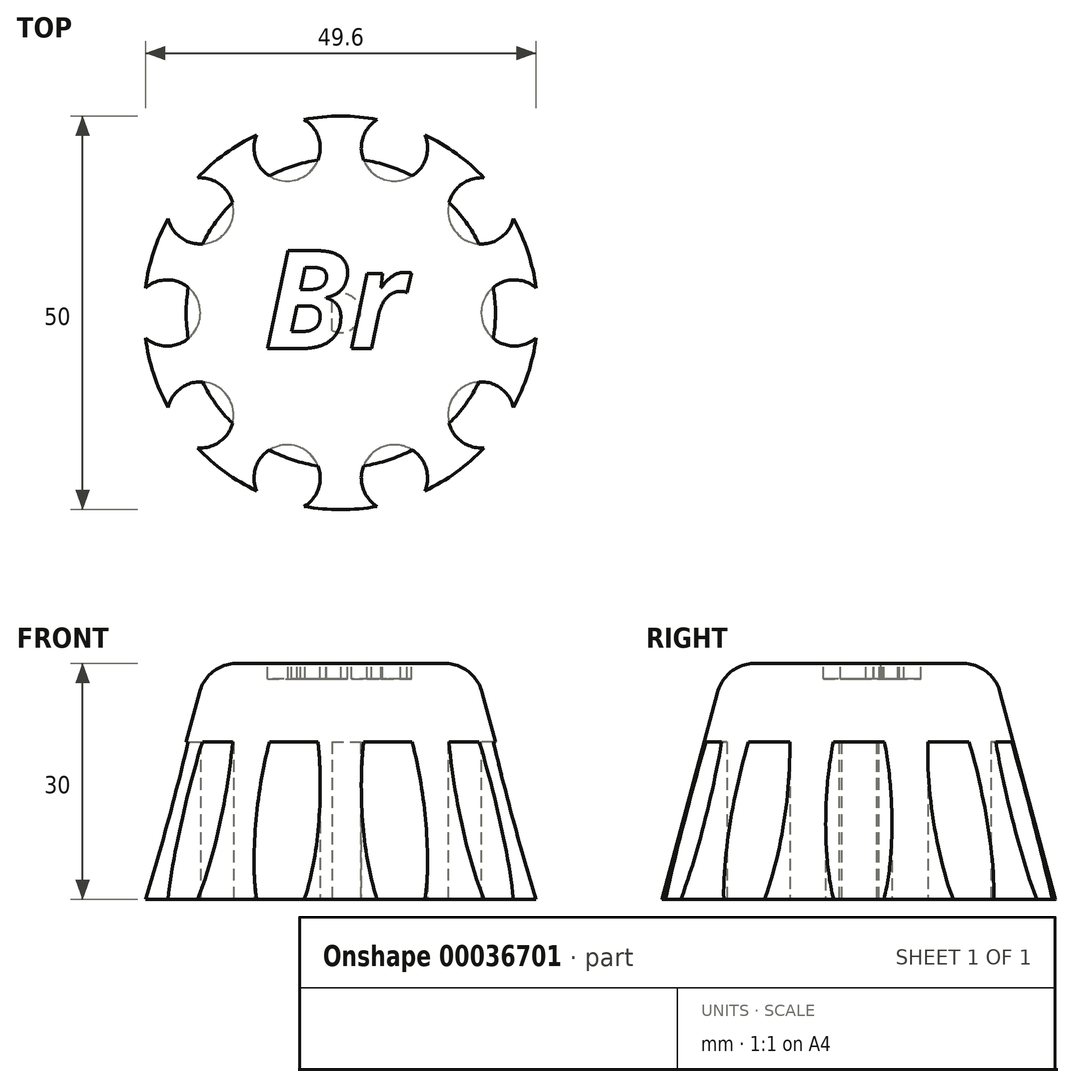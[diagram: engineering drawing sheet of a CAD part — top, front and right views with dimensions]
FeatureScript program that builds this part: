
annotation { "Feature Type Name" : "Feature", "Feature Type Description" : "" }
export const myFeature = defineFeature(function(context is Context, id is Id, definition is map)
    precondition{}
    {
        {
            var Q0;
            Q0=qCreatedBy(makeId("Top.planeOp"),FACE);
            var sketch = newSketch(context, id + "F0", { "sketchPlane" : qUnion([Q0])});
            skCircle(sketch, "E0", {"center": v(0, 0) * mm, "radius": 25 * mm});
            skSolve(sketch);
        }
        {
            var Q0;
            Q0=qSketchRegion(id+"F0",true);
            extrude(context, id + "F1", {"entities" : qUnion([Q0]), "depth" : 30 * mm, "hasDraft" : true, "draftAngle" : 15 * degree, "draftPullDirection" : true});
        }
        {
            var Q0;
            Q0=qCreatedBy(makeId("Top.planeOp"),FACE);
            var sketch = newSketch(context, id + "F2", { "sketchPlane" : qUnion([Q0])});
            skArc(sketch, "E1", {"start": v(-1.13, -2.23) * mm, "mid": v(2.5, 0) * mm, "end": v(-1.13, 2.23) * mm});
            skLineSegment(sketch, "E2", {"start": v(-1.13, -2.23) * mm, "end": v(-1.13, 2.23) * mm});
            skSolve(sketch);
        }
        {
            var Q0;
            Q0=qSketchRegion(id+"F2",true);
            extrude(context, id + "F3", {"entities" : qUnion([Q0]), "operationType" : NewBodyOperationType.REMOVE, "depth" : 20 * mm});
        }
        {
            var Q0;
            Q0=qCreatedBy(makeId("Top.planeOp"),FACE);
            var sketch = newSketch(context, id + "F4", { "sketchPlane" : qUnion([Q0])});
            skPoint(sketch, "E3.center", {"position": v(0, 0) * mm});
            skCircle(sketch, "E4", {"center": v(0, 0) * mm, "radius": 22.04 * mm, "construction": true});
            skCircle(sketch, "E5", {"center": v(22.04, 0) * mm, "radius": 4.2 * mm});
            skCircle(sketch, "E6.1.0", {"center": v(17.83, 12.96) * mm, "radius": 4.2 * mm});
            skCircle(sketch, "E6.2.0", {"center": v(6.81, 20.96) * mm, "radius": 4.2 * mm});
            skCircle(sketch, "E6.3.0", {"center": v(-6.81, 20.96) * mm, "radius": 4.2 * mm});
            skCircle(sketch, "E6.4.0", {"center": v(-17.83, 12.96) * mm, "radius": 4.2 * mm});
            skCircle(sketch, "E6.5.0", {"center": v(-22.04, 0) * mm, "radius": 4.2 * mm});
            skCircle(sketch, "E6.6.0", {"center": v(-17.83, -12.96) * mm, "radius": 4.2 * mm});
            skCircle(sketch, "E6.7.0", {"center": v(-6.81, -20.96) * mm, "radius": 4.2 * mm});
            skCircle(sketch, "E6.8.0", {"center": v(6.81, -20.96) * mm, "radius": 4.2 * mm});
            skCircle(sketch, "E6.9.0", {"center": v(17.83, -12.96) * mm, "radius": 4.2 * mm});
            skSolve(sketch);
        }
        {
            var Q0;
            Q0=makeQuery(id+"F1.opExtrude","CAP_EDGE",EDGE,{"disambiguationData":[OSD([sQuery(id+"F0.wireOp",EDGE,"E0")])],"isStart":false});
            fillet(context, id + "F5", {"entities" : qUnion([Q0]), "radius" : 5 * mm, "tangentPropagation" : true, "allowEdgeOverflow" : false});
        }
        {
            var Q0;
            Q0=qSketchRegion(id+"F4",true);
            extrude(context, id + "F6", {"entities" : qUnion([Q0]), "operationType" : NewBodyOperationType.REMOVE, "depth" : 20 * mm});
        }
        {
            var Q0;
            Q0=makeQuery(id+"F1.opExtrude","CAP_FACE",FACE,{"disambiguationData":[OSD([sQuery(id+"F0.wireOp",EDGE,"E0")])],"isStart":false});
            var sketch = newSketch(context, id + "F7", { "sketchPlane" : qUnion([Q0])});
            skText(sketch, "E7", { "text": "Br", "fontName": "OpenSans-BoldItalic.ttf"});
            const initialGuessF7  = {"E7": [-0.00977, -0.00452, 1, 0, 0.01253]};
            skSetInitialGuess(sketch, initialGuessF7);
            skSolve(sketch);
        }
        {
            var Q0;
            Q0=qSketchRegion(id+"F7",true);
            extrude(context, id + "F8", {"entities" : qUnion([Q0]), "operationType" : NewBodyOperationType.REMOVE, "oppositeDirection" : true, "depth" : 2 * mm});
        }
    });
